# Revit family: Haworth_CabanaLounge_Table_Wedge
name_source: partatom
category: Furniture
revit_build: Autodesk Revit 2018 (Build: 20170223_1515(x64)
units: mm (PartAtom-declared; Revit-internal decimal feet)

## family parameters
Always vertical = Yes
Cut with Voids When Loaded = No
OmniClass Number = 23.40.70.14.64.21
OmniClass Title = Systems Furniture
Room Calculation Point = No
Shared = No
Work Plane-Based = No

## types (6) — shared parameters
Actual Depth = 32"
Actual Width = 30"
Assembly Code = E2020200
Manufacturer = Haworth
Model = Haworth Cabana
Revision Number = 1
Screen Width = 30"
Size = Verify Final Dim. w/ Haworth
Table Depth = 32"
Table Width = 28"
URL = http://www.haworth.com
URL - Product = https://www.haworth.com
Warranty = http://www.haworth.com

## per-type parameters (varying)
| type | Actual Height | Description | High Screen | Low Screen | No Screen | Screen Control | Table Height | With Screen | With Top |
| S966 - Wedge Tiered - High Screen | 54" | Haworth Cabana Table - Wedge Tiered - High Screen | Yes | No | No | 2" | 15 11/16" | Yes | Yes |
| S965 - Wedge Tiered - Low Screen | 42" | Haworth Cabana Table - Wedge Tiered - Low Screen | No | Yes | No | 2" | 15 11/16" | Yes | Yes |
| S960 - Wedge Tiered - No Screen | 15 11/16" | Haworth Cabana Table - Wedge Tiered - No Screen | No | No | Yes | 0" | 15 11/16" | No | Yes |
| S950 - Wedge - No Screen | 11 5/16" | Haworth Cabana Table - Wedge - No Screen | No | No | Yes | 0" | 11 5/16" | No | No |
| S955 - Wedge - Low Screen | 42" | Haworth Cabana Table - Wedge - Low Screen | No | Yes | No | 2" | 11 5/16" | Yes | No |
| S956 - Wedge - High Screen | 54" | Haworth Cabana Table - Wedge - High Screen | Yes | No | No | 2" | 11 5/16" | Yes | No |

## geometry (parser evidence)
native form markers: Sweep x11
no freeform markers — native parametric forms only
